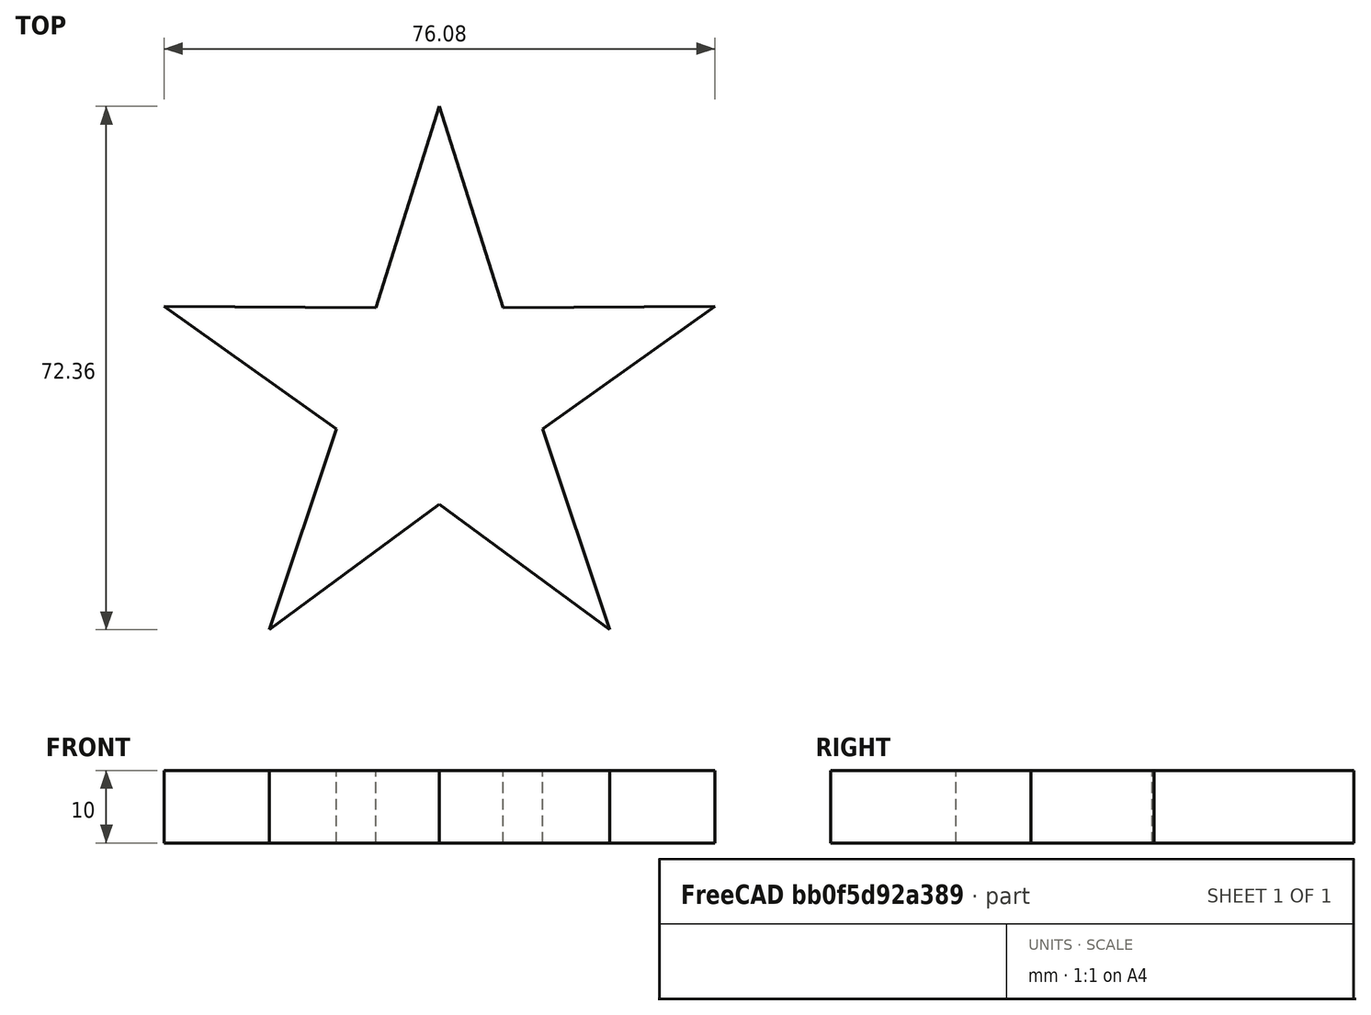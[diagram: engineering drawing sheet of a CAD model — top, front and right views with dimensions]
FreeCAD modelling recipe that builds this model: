
FCSTD DOCUMENT  (FreeCAD 0.21R33694 (Git))
Label: OJT1_T20R03.estrella
License: All rights reserved
LicenseURL: http://en.wikipedia.org/wiki/All_rights_reserved
objects: Sketcher::SketchObject×1, PartDesign::Pad×1, PartDesign::Body×1, App::Part×1
note: 4 computed .brp shape members not serialized (recipe doc carries the construction recipe); baked Part::Feature solids carry a one-line shape summary decoded from their .brp

FEATURE [Sketcher::SketchObject] Sketch
  FullyConstrained = true
  MapMode = 5
  Support = -> [XY_Plane001]
  sketch-geometry (14):
    g0: LineSegment StartX=0 StartY=40 StartZ=0 EndX=8.81678 EndY=12.1353 EndZ=0
    g1: LineSegment StartX=8.81678 StartY=12.1353 StartZ=0 EndX=38.0423 EndY=12.3607 EndZ=0
    g2: LineSegment StartX=38.0423 StartY=12.3607 StartZ=0 EndX=14.2658 EndY=-4.63525 EndZ=0
    g3: LineSegment StartX=14.2658 StartY=-4.63525 StartZ=0 EndX=23.5114 EndY=-32.3607 EndZ=0
    g4: LineSegment StartX=23.5114 StartY=-32.3607 StartZ=0 EndX=0 EndY=-15 EndZ=0
    g5: LineSegment StartX=0 StartY=-15 StartZ=0 EndX=-23.5114 EndY=-32.3607 EndZ=0
    g6: LineSegment StartX=-23.5114 StartY=-32.3607 StartZ=0 EndX=-14.2658 EndY=-4.63525 EndZ=0
    g7: LineSegment StartX=-14.2658 StartY=-4.63525 StartZ=0 EndX=-38.0423 EndY=12.3607 EndZ=0
    g8: LineSegment StartX=-38.0423 StartY=12.3607 StartZ=0 EndX=-8.81678 EndY=12.1353 EndZ=0
    g9: LineSegment StartX=-8.81678 StartY=12.1353 StartZ=0 EndX=0 EndY=40 EndZ=0
    g10: LineSegment StartX=0 StartY=-15 StartZ=0 EndX=0 EndY=0 EndZ=0
    g11: LineSegment StartX=0 StartY=0 StartZ=0 EndX=-14.2658 EndY=-4.63525 EndZ=0
    g12: LineSegment StartX=0 StartY=0 StartZ=0 EndX=0 EndY=40 EndZ=0
    g13: LineSegment StartX=-8.81678 StartY=12.1353 StartZ=0 EndX=0 EndY=0 EndZ=0
  constraints (36):
    c: PointOnObject(g0,g-2)
    c: Coincident(g0,g1)
    c: Coincident(g1,g2)
    c: Coincident(g2,g3)
    c: Coincident(g3,g4)
    c: PointOnObject(g4,g-2)
    c: Coincident(g4,g5)
    c: Coincident(g5,g6)
    c: Coincident(g6,g7)
    c: Coincident(g7,g8)
    c: Coincident(g8,g9)
    c: Coincident(g9,g0)
    c: Symmetric(g1,g7,g-2)
    c: Symmetric(g5,g3,g-2)
    c: Equal(g6,g5)
    c: Equal(g5,g7)
    c: Equal(g7,g8)
    c: Equal(g8,g9)
    c: Equal(g9,g0)
    c: Equal(g0,g1)
    c: Equal(g1,g2)
    c: Equal(g3,g4)
    c: Coincident(g10,g4)
    c: Coincident(g10,g-1)
    c: Coincident(g11,g10)
    c: Coincident(g11,g6)
    c: Equal(g11,g10)
    c: Angle(g11,g10) = 1.25664
    c: Coincident(g12,g10)
    c: Coincident(g12,g0)
    c: Distance(g12) = 40
    c: DistanceY(g10,g10) = 15
    c: Coincident(g13,g8)
    c: Coincident(g13,g12)
    c: Angle(g13,g11) = 1.25664
    c: Equal(g11,g13)
FEATURE [PartDesign::Pad] Pad
  Direction = (0,0,1)
  Length = 10
  Length2 = 10
  Profile = -> Sketch
  ReferenceAxis = -> Sketch [N_Axis]
  Refine = true
  Type = 0
FEATURE [PartDesign::Body] Body  label="Cos"
  Group = -> [Sketch,Pad]
  Origin = -> Origin001
  Tip = -> Pad
FEATURE [App::Part] Part
  Group = -> [Body]
  Origin = -> Origin
